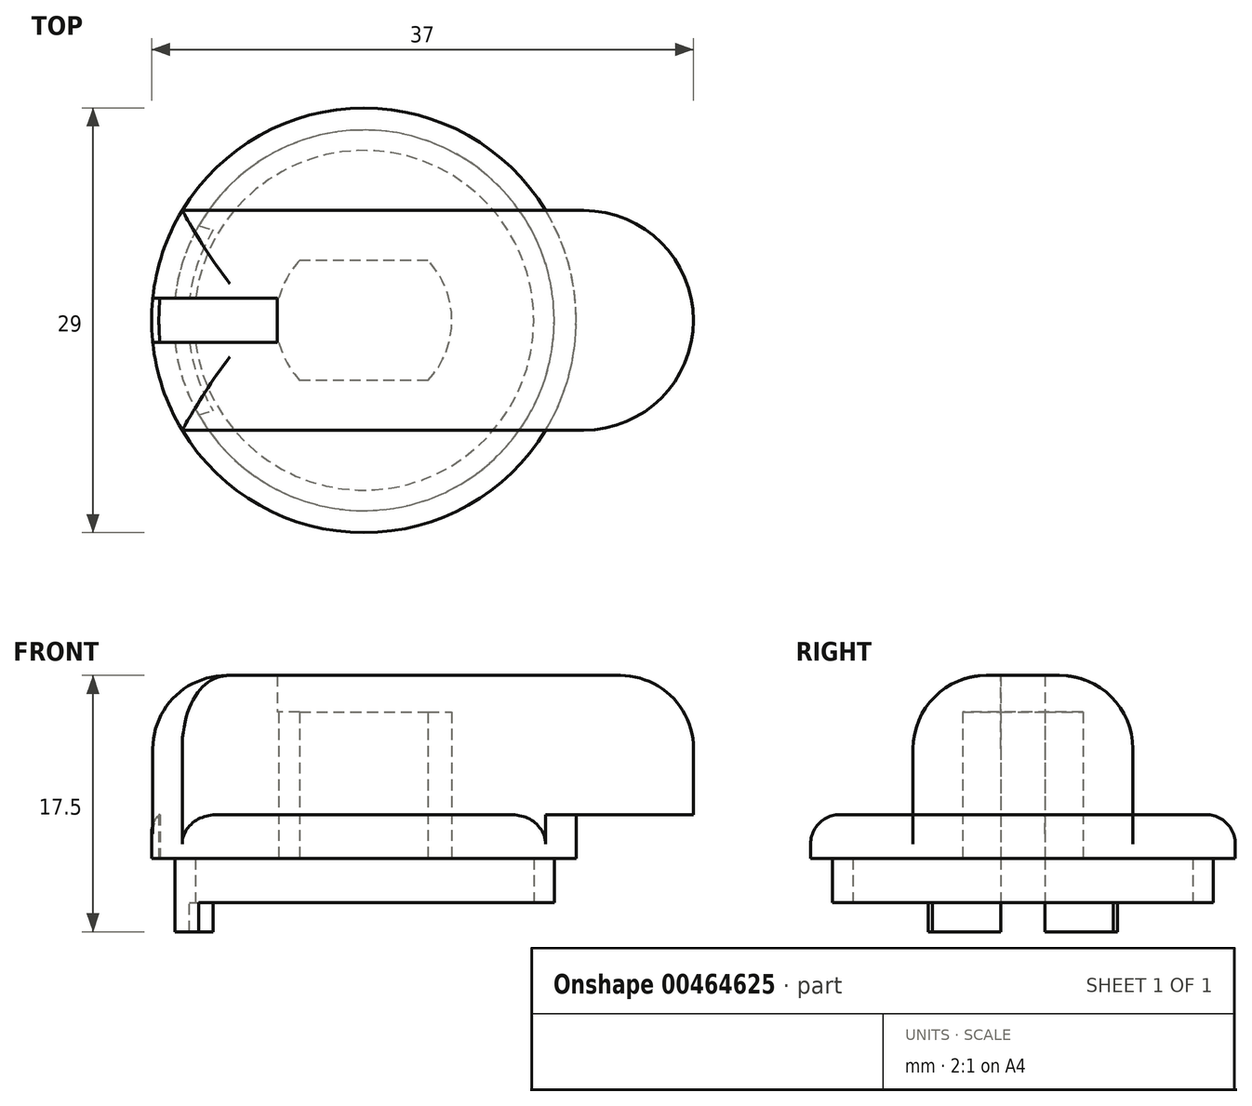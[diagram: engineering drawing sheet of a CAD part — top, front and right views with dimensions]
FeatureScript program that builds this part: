
annotation { "Feature Type Name" : "Feature", "Feature Type Description" : "" }
export const myFeature = defineFeature(function(context is Context, id is Id, definition is map)
    precondition{}
    {
        {
            var Q0;
            Q0=qCreatedBy(makeId("Top.planeOp"),FACE);
            var sketch = newSketch(context, id + "F0", { "sketchPlane" : qUnion([Q0])});
            skCircle(sketch, "E0", {"center": v(0, 0) * mm, "radius": 13 * mm});
            skCircle(sketch, "E1.0", {"center": v(0, 0) * mm, "radius": 11.6 * mm});
            skSolve(sketch);
        }
        {
            var Q0;
            Q0=makeQuery(id+"F0.imprint","IMPRINT",FACE,{"disambiguationData":[TD([[makeQuery(id+"F0.imprint","IMPRINT",EDGE,{"derivedFrom":sQuery(id+"F0.wireOp",EDGE,"E0")}),1.0]])]});
            extrude(context, id + "F1", {"entities" : qUnion([Q0]), "depth" : 3 * mm});
        }
        {
            var Q0;
            Q0=makeQuery(id+"F1.opExtrude","CAP_FACE",FACE,{"disambiguationData":[OSD([sQuery(id+"F0.wireOp",EDGE,"E0"),sQuery(id+"F0.wireOp",EDGE,"E1.0")])],"isStart":false});
            var sketch = newSketch(context, id + "F2", { "sketchPlane" : qUnion([Q0])});
            skCircle(sketch, "E2", {"center": v(0, 0) * mm, "radius": 14.5 * mm});
            skSolve(sketch);
        }
        {
            var Q0;
            Q0=makeQuery(id+"F2.imprint","IMPRINT",FACE,{"disambiguationData":[TD([[makeQuery(id+"F2.imprint","IMPRINT",EDGE,{"derivedFrom":makeQuery(id+"F1.opExtrude","CAP_EDGE",EDGE,{"disambiguationData":[OSD([sQuery(id+"F0.wireOp",EDGE,"E1.0")])],"isStart":false})}),1.0]])]});
            var Q1;
            Q1=makeQuery(id+"F2.imprint","IMPRINT",FACE,{"disambiguationData":[TD([[makeQuery(id+"F2.imprint","IMPRINT",EDGE,{"derivedFrom":makeQuery(id+"F1.opExtrude","CAP_EDGE",EDGE,{"disambiguationData":[OSD([sQuery(id+"F0.wireOp",EDGE,"E0")])],"isStart":false})}),1.0]])]});
            var Q2;
            Q2=makeQuery(id+"F2.imprint","IMPRINT",FACE,{"disambiguationData":[TD([[makeQuery(id+"F2.imprint","IMPRINT",EDGE,{"derivedFrom":sQuery(id+"F2.wireOp",EDGE,"E2")}),1.0]])]});
            extrude(context, id + "F3", {"entities" : qUnion([Q0, Q1, Q2]), "operationType" : NewBodyOperationType.ADD, "depth" : 3 * mm});
        }
        {
            var Q0;
            Q0=makeQuery(id+"F3.opExtrude","CAP_FACE",FACE,{"disambiguationData":[OSD([sQuery(id+"F2.wireOp",EDGE,"E2")])],"isStart":false});
            var sketch = newSketch(context, id + "F4", { "sketchPlane" : qUnion([Q0])});
            skLineSegment(sketch, "E3", {"start": v(-16.77, 0) * mm, "end": v(26.85, 0) * mm, "construction": true});
            skLineSegment(sketch, "E4", {"start": v(-12.4, 7.5) * mm, "end": v(15, 7.5) * mm});
            skLineSegment(sketch, "E5", {"start": v(22.5, 0) * mm, "end": v(22.5, 0) * mm});
            skArc(sketch, "E6", {"start": v(-12.4, 7.5) * mm, "mid": v(-13.75, 4.61) * mm, "end": v(-14.42, 1.5) * mm});
            skPoint(sketch, "E7.visualSharp", {"position": v(22.5, 7.5) * mm});
            skArc(sketch, "E7.filletArc", {"start": v(22.5, 0) * mm, "mid": v(20.3, 5.3) * mm, "end": v(15, 7.5) * mm});
            skLineSegment(sketch, "E8", {"start": v(-14.42, 1.5) * mm, "end": v(-5.92, 1.5) * mm});
            skLineSegment(sketch, "E9", {"start": v(-5.92, 1.5) * mm, "end": v(-5.92, 0) * mm});
            skPoint(sketch, "E10.orphan", {"position": v(-14.5, 0) * mm});
            skPoint(sketch, "E11.MirrorP", {"position": v(22.5, -7.5) * mm});
            skLineSegment(sketch, "E12.MirrorCS", {"start": v(-12.4, -7.5) * mm, "end": v(15, -7.5) * mm});
            skArc(sketch, "E13.MirrorCS", {"start": v(-12.4, -7.5) * mm, "mid": v(-13.75, -4.61) * mm, "end": v(-14.42, -1.5) * mm});
            skLineSegment(sketch, "E14.MirrorCS", {"start": v(-14.42, -1.5) * mm, "end": v(-5.92, -1.5) * mm});
            skLineSegment(sketch, "E15.MirrorCS", {"start": v(-5.92, -1.5) * mm, "end": v(-5.92, 0) * mm});
            skArc(sketch, "E16.MirrorCS", {"start": v(22.5, 0) * mm, "mid": v(20.3, -5.3) * mm, "end": v(15, -7.5) * mm});
            skSolve(sketch);
        }
        {
            var Q0;
            {var subQ5=sQuery(id+"F4.wireOp",EDGE,"E6");Q0=makeQuery(id+"F4.imprint","IMPRINT",FACE,{"disambiguationData":[TD([[makeQuery(id+"F4.imprint","IMPRINT",EDGE,{"derivedFrom":subQ5}),1.0]])]});}
            var Q1;
            {var subQ4=sQuery(id+"F4.wireOp",EDGE,"E7.filletArc");Q1=makeQuery(id+"F4.imprint","IMPRINT",FACE,{"disambiguationData":[TD([[makeQuery(id+"F4.imprint","IMPRINT",EDGE,{"derivedFrom":subQ4}),1.0]])]});}
            extrude(context, id + "F5", {"entities" : qUnion([Q0, Q1]), "operationType" : NewBodyOperationType.ADD, "depth" : 9.5 * mm});
        }
        {
            var Q0;
            Q0=makeQuery(id+"F1.opExtrude","CAP_FACE",FACE,{"disambiguationData":[OSD([sQuery(id+"F0.wireOp",EDGE,"E0"),sQuery(id+"F0.wireOp",EDGE,"E1.0")])],"isStart":true});
            var sketch = newSketch(context, id + "F6", { "sketchPlane" : qUnion([Q0])});
            skLineSegment(sketch, "E17", {"start": v(-14.7, 0) * mm, "end": v(3.76, 0) * mm, "construction": true});
            skArc(sketch, "E18", {"start": v(-11.28, 6.46) * mm, "mid": v(-13, 0) * mm, "end": v(-11.28, -6.46) * mm});
            skArc(sketch, "E19", {"start": v(-10.3, 6.17) * mm, "mid": v(-12, 0) * mm, "end": v(-10.3, -6.17) * mm});
            skLineSegment(sketch, "E20", {"start": v(-11.28, 6.46) * mm, "end": v(-10.3, 6.17) * mm});
            skLineSegment(sketch, "E21", {"start": v(-11.28, -6.46) * mm, "end": v(-10.3, -6.17) * mm});
            skPoint(sketch, "E22.orphan", {"position": v(-9.73, 6) * mm});
            skPoint(sketch, "E23.orphan", {"position": v(-11.4, 6.5) * mm});
            skPoint(sketch, "E24.orphan", {"position": v(-9.73, -6) * mm});
            skPoint(sketch, "E25.orphan", {"position": v(-11.4, -6.5) * mm});
            skSolve(sketch);
        }
        {
            var Q0;
            Q0=makeQuery(id+"F6.imprint","IMPRINT",FACE,{"disambiguationData":[TD([[makeQuery(id+"F6.imprint","IMPRINT",EDGE,{"derivedFrom":sQuery(id+"F6.wireOp",EDGE,"E18")}),-1.0]])]});
            extrude(context, id + "F7", {"entities" : qUnion([Q0]), "operationType" : NewBodyOperationType.ADD, "depth" : 2 * mm});
        }
        {
            var Q0;
            Q0=makeQuery(id+"F3.boolean.opBoolean","SPLIT",FACE,{"disambiguationData":[TD([makeQuery(id+"F1.opExtrude","SWEPT_FACE",FACE,{"disambiguationData":[OSD([sQuery(id+"F0.wireOp",EDGE,"E1.0")])]})])],"derivedFrom":makeQuery(id+"F3.opExtrude","CAP_FACE",FACE,{"disambiguationData":[OSD([sQuery(id+"F2.wireOp",EDGE,"E2")])],"isStart":true})});
            var sketch = newSketch(context, id + "F8", { "sketchPlane" : qUnion([Q0])});
            skLineSegment(sketch, "E26", {"start": v(-17.61, 0) * mm, "end": v(24, 0) * mm, "construction": true});
            skArc(sketch, "E27", {"start": v(-5.8, -1.5) * mm, "mid": v(-5.26, -2.89) * mm, "end": v(-4.38, -4.1) * mm});
            skLineSegment(sketch, "E28", {"start": v(-4.38, -4.1) * mm, "end": v(4.38, -4.1) * mm});
            skLineSegment(sketch, "E29", {"start": v(-4.38, 4.1) * mm, "end": v(4.38, 4.1) * mm});
            skArc(sketch, "E30.trimOffspring", {"start": v(4.38, -4.1) * mm, "mid": v(6, 0) * mm, "end": v(4.38, 4.1) * mm});
            skArc(sketch, "E31.trimOffspring", {"start": v(-4.38, 4.1) * mm, "mid": v(-5.26, 2.89) * mm, "end": v(-5.8, 1.5) * mm});
            skArc(sketch, "E32", {"start": v(-13.92, 1.5) * mm, "mid": v(-14, 0) * mm, "end": v(-13.92, -1.5) * mm});
            skLineSegment(sketch, "E33", {"start": v(-5.8, 1.5) * mm, "end": v(-13.92, 1.5) * mm});
            skLineSegment(sketch, "E34", {"start": v(-5.8, -1.5) * mm, "end": v(-13.92, -1.5) * mm});
            skSolve(sketch);
        }
        {
            var Q0;
            Q0=makeQuery(id+"F5.opExtrude","CAP_EDGE",EDGE,{"disambiguationData":[OSD([sQuery(id+"F4.wireOp",EDGE,"E12.MirrorCS")])],"isStart":false});
            var Q1;
            Q1=makeQuery(id+"F5.opExtrude","CAP_EDGE",EDGE,{"disambiguationData":[OSD([sQuery(id+"F4.wireOp",EDGE,"E13.MirrorCS")])],"isStart":false});
            var Q2;
            Q2=makeQuery(id+"F5.opExtrude","CAP_EDGE",EDGE,{"disambiguationData":[OSD([sQuery(id+"F4.wireOp",EDGE,"E6")])],"isStart":false});
            fillet(context, id + "F9", {"entities" : qUnion([Q0, Q1, Q2]), "radius" : 5 * mm, "tangentPropagation" : true, "allowEdgeOverflow" : false});
        }
        {
            var Q0;
            {var subQ0=sQuery(id+"F8.wireOp",EDGE,"E27");Q0=makeQuery(id+"F8.imprint","IMPRINT",FACE,{"disambiguationData":[TD([[makeQuery(id+"F8.imprint","IMPRINT",EDGE,{"derivedFrom":subQ0}),1.0]])]});}
            var Q1;
            {var subQ0=sQuery(id+"F8.wireOp",EDGE,"E32");Q1=makeQuery(id+"F8.imprint","IMPRINT",FACE,{"disambiguationData":[TD([[makeQuery(id+"F8.imprint","IMPRINT",EDGE,{"derivedFrom":subQ0}),1.0]])]});}
            extrude(context, id + "F10", {"entities" : qUnion([Q0, Q1]), "operationType" : NewBodyOperationType.REMOVE, "oppositeDirection" : true, "depth" : 10 * mm, "hasSecondDirection" : true, "secondDirectionOppositeDirection" : false, "secondDirectionDepth" : 10 * mm});
        }
        {
            var Q0;
            {var subQ0=sQuery(id+"F4.wireOp",EDGE,"E4");var subQ1=sQuery(id+"F2.wireOp",EDGE,"E2");var subQ2=makeQuery(id+"F3.opExtrude","CAP_FACE",FACE,{"disambiguationData":[OSD([subQ1])],"isStart":false});var subQ3=sQuery(id+"F4.wireOp",EDGE,"E13.MirrorCS");var subQ4=makeQuery(id+"F5.opExtrude","SWEPT_FACE",FACE,{"disambiguationData":[OSD([subQ3])]});var subQ5=sQuery(id+"F4.wireOp",EDGE,"E6");var subQ6=makeQuery(id+"F3.opExtrude","SWEPT_FACE",FACE,{"disambiguationData":[OSD([subQ1])]});var subQ7=makeQuery(id+"F5.opExtrude","SWEPT_FACE",FACE,{"disambiguationData":[OSD([subQ5])]});Q0=makeQuery(id+"F5.boolean.opBoolean","SPLIT",EDGE,{"disambiguationData":[topologyDisambiguationEdgeConnected([subQ6,subQ2,subQ7,subQ4]),TD([makeQuery(id+"F5.opExtrude","SWEPT_FACE",FACE,{"disambiguationData":[OSD([subQ0])]})])],"derivedFrom":makeQuery(id+"F3.opExtrude","CAP_EDGE",EDGE,{"disambiguationData":[OSD([subQ1])],"isStart":false})});}
            var Q1;
            {var subQ0=sQuery(id+"F4.wireOp",EDGE,"E6");var subQ1=makeQuery(id+"F5.opExtrude","SWEPT_FACE",FACE,{"disambiguationData":[OSD([subQ0])]});var subQ2=sQuery(id+"F2.wireOp",EDGE,"E2");var subQ3=makeQuery(id+"F3.opExtrude","CAP_FACE",FACE,{"disambiguationData":[OSD([subQ2])],"isStart":false});var subQ4=sQuery(id+"F4.wireOp",EDGE,"E13.MirrorCS");var subQ5=makeQuery(id+"F5.opExtrude","SWEPT_FACE",FACE,{"disambiguationData":[OSD([subQ4])]});var subQ6=sQuery(id+"F4.wireOp",EDGE,"E12.MirrorCS");var subQ7=makeQuery(id+"F3.opExtrude","SWEPT_FACE",FACE,{"disambiguationData":[OSD([subQ2])]});Q1=makeQuery(id+"F5.boolean.opBoolean","SPLIT",EDGE,{"disambiguationData":[topologyDisambiguationEdgeConnected([subQ7,subQ3,subQ1,subQ5]),TD([makeQuery(id+"F5.opExtrude","SWEPT_FACE",FACE,{"disambiguationData":[OSD([subQ6])]})])],"derivedFrom":makeQuery(id+"F3.opExtrude","CAP_EDGE",EDGE,{"disambiguationData":[OSD([subQ2])],"isStart":false})});}
            fillet(context, id + "F11", {"entities" : qUnion([Q0, Q1]), "radius" : 2 * mm, "tangentPropagation" : true, "allowEdgeOverflow" : false});
        }
    });
